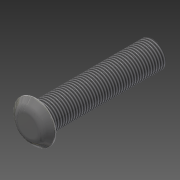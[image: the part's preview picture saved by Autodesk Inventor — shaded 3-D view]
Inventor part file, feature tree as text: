
AUTODESK INVENTOR PART (.ipt)
format: ipt  version: 2015 (Build 190159000, 159)  size: 139,776 bytes
history: native  units: mm
features: sketch x3, other x2, extrude x1, thread x1, hole x1
ambient origin geometry x8: Origin, YZ Plane, XZ Plane, XY Plane, X Axis, Y Axis, Z Axis, Center Point
bodies: Body1 (feature_tree)
feature tree (8):
  other  "Bryła1"
  extrude  "Wyciągnięcie proste1"  Depth=8.0mm
  other  "Podstawa"
  thread  "Gwint1"
  hole  "Otwór1"  [1 undecoded]
  sketch  "Szkic1"
  sketch  "Szkic3"
  sketch  "Szkic4"
note: 1 required parameter value undecoded (feature->parameter linkage not recoverable at this tier; creation-order binding heuristic only, values carry confidence <= 0.55)
